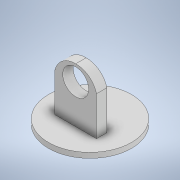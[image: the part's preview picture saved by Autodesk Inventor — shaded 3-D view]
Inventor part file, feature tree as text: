
AUTODESK INVENTOR PART (.ipt)
format: ipt  version: 2022 (Build 260153000, 153)  size: 135,680 bytes
history: native  units: in
note: dims shown in document units (in); Inventor stores cm internally (conversion verified against a paired STEP export)
features: sketch x4, extrude x3
ambient origin geometry x8: Origin, YZ Plane, XZ Plane, XY Plane, X Axis, Y Axis, Z Axis, Center Point
bodies: Solid1 (feature_tree)
feature tree (7):
  extrude  "Extrusion1"  Depth=0.5906in
  extrude  "Extrusion2"  Depth=1.5748in
  extrude  "Extrusion3"  Depth=1.5748in
  sketch  "Sketch4"  dims[d7=5.9055in d8=0.0in d9=1.9685in d10=1.7717in d11=1.5748in d12=1.5748in d13=0.8445in d14=0.0in]
  sketch  "Sketch1"  dims[d0=6.2992in d1=0.5906in]
  sketch  "Sketch2"  dims[d2=0.3937in d3=0.0in d4=1.5748in]
  sketch  "Sketch3"  dims[d5=0.7874in d6=1.5748in]
